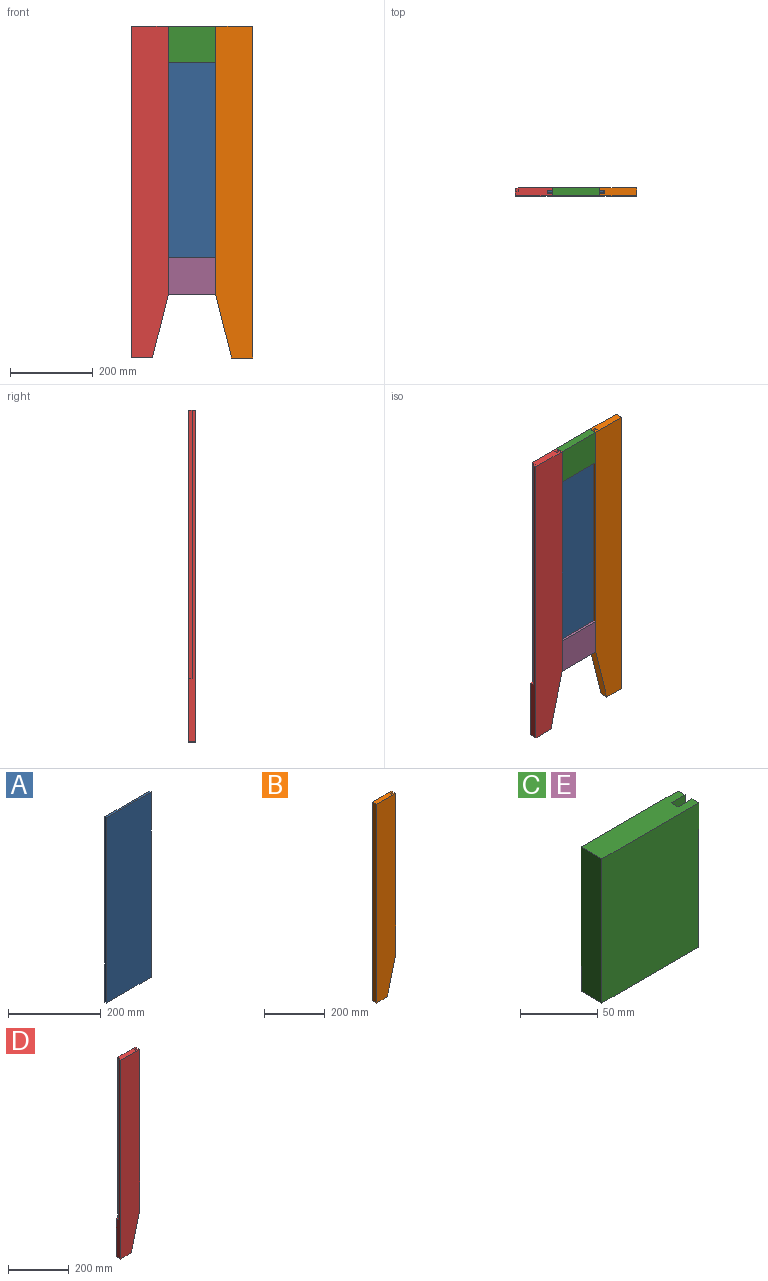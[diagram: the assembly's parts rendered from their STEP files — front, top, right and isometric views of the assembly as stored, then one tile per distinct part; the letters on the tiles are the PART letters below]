
ASSEMBLY  parts=5 mates=4
PART A: 6 faces, bbox 136.5x5.1x489 mm
  f0: plane 136.53x5.08mm, normal (0,0,1), area 693.5mm2, adj f1,f3,f4,f5
  f1: plane 488.95x5.08mm, normal (-1,0,0), area 2483.9mm2, adj f0,f2,f4,f5
  f2: plane 136.53x5.08mm, normal (0,0,-1), area 693.5mm2, adj f1,f3,f4,f5
  f3: plane 488.95x5.08mm, normal (1,0,0), area 2483.9mm2, adj f0,f2,f4,f5
  f4: plane 488.95x136.53mm, normal (0,-1,0), area 66753.9mm2, adj f0,f1,f2,f3
  f5: plane 488.95x136.53mm, normal (0,1,0), area 66753.9mm2, adj f0,f1,f2,f3
PART B: 12 faces, bbox 88.9x19.1x800.1 mm
  f0: plane 647.7x6.35mm, normal (1,0,0), area 4112.9mm2, adj f3,f5,f7,f10
  f1: plane 50.8x19.05mm, normal (0,0,-1), area 967.7mm2, adj f2,f3,f6,f7
  f2: plane 800.1x88.9mm, normal (0,-1,0), area 68225.7mm2, adj f1,f4,f5,f6,f7
  f3: plane 800.1x88.9mm, normal (0,1,0), area 68225.7mm2, adj f0,f1,f5,f6,f7
  f4: plane 647.7x6.35mm, normal (1,0,0), area 4112.9mm2, adj f2,f5,f7,f8
  f5: plane 88.9x19.05mm, normal (0,0,1), area 1612.9mm2, adj f0,f2,f3,f4,f6,f8,f10,f11
  f6: plane 800.1x19.05mm, normal (-1,0,0), area 15241.9mm2, adj f1,f2,f3,f5
  f7: plane 152.4x38.1mm, normal (0.97,0,-0.24), area 2992.6mm2, adj f0,f1,f2,f3,f4,f9
  f8: plane 647.7x12.7mm, normal (0,1,0), area 8225.8mm2, adj f4,f5,f9,f11
  f9: plane 12.7x6.35mm, normal (0,0,1), area 80.6mm2, adj f7,f8,f10,f11
  f10: plane 647.7x12.7mm, normal (0,-1,0), area 8225.8mm2, adj f0,f5,f9,f11
  f11: plane 647.7x6.35mm, normal (1,0,0), area 4112.9mm2, adj f5,f8,f9,f10
PART C: 10 faces, bbox 88.9x19.1x114.3 mm
  f0: plane 114.3x6.35mm, normal (1,0,0), area 725.8mm2, adj f1,f3,f5,f7
  f1: plane 88.9x19.05mm, normal (0,0,-1), area 1612.9mm2, adj f0,f2,f4,f5,f6,f7,f8,f9
  f2: plane 114.3x6.35mm, normal (1,0,0), area 725.8mm2, adj f1,f3,f6,f8
  f3: plane 88.9x19.05mm, normal (0,0,1), area 1612.9mm2, adj f0,f2,f4,f5,f6,f7,f8,f9
  f4: plane 114.3x19.05mm, normal (-1,0,0), area 2177.4mm2, adj f1,f3,f5,f6
  f5: plane 114.3x88.9mm, normal (0,-1,0), area 10161.3mm2, adj f0,f1,f3,f4
  f6: plane 114.3x88.9mm, normal (0,1,0), area 10161.3mm2, adj f1,f2,f3,f4
  f7: plane 114.3x12.7mm, normal (0,1,0), area 1451.6mm2, adj f0,f1,f3,f9
  f8: plane 114.3x12.7mm, normal (0,-1,0), area 1451.6mm2, adj f1,f2,f3,f9
  f9: plane 114.3x6.35mm, normal (1,0,0), area 725.8mm2, adj f1,f3,f7,f8
PART D: 15 faces, bbox 88.9x19.1x800.1 mm
  f0: plane 800.1x88.9mm, normal (0,1,0), area 64112.8mm2, adj f1,f2,f5,f6,f7,f12,f13
  f1: plane 647.7x6.35mm, normal (1,0,0), area 4112.9mm2, adj f0,f5,f7,f10
  f2: plane 50.8x19.05mm, normal (0,0,-1), area 967.7mm2, adj f0,f3,f6,f7
  f3: plane 800.1x88.9mm, normal (0,-1,0), area 68225.7mm2, adj f2,f4,f5,f6,f7
  f4: plane 647.7x6.35mm, normal (1,0,0), area 4112.9mm2, adj f3,f5,f7,f8
  f5: plane 88.9x19.05mm, normal (0,0,1), area 1552.4mm2, adj f0,f1,f3,f4,f6,f8,f10,f11
  f6: plane 800.1x19.05mm, normal (-1,0,0), area 9072.6mm2, adj f0,f2,f3,f5,f13,f14
  f7: plane 152.4x38.1mm, normal (0.97,0,-0.24), area 2992.6mm2, adj f0,f1,f2,f3,f4,f9
  f8: plane 647.7x12.7mm, normal (0,1,0), area 8225.8mm2, adj f4,f5,f9,f11
  f9: plane 12.7x6.35mm, normal (0,0,1), area 80.6mm2, adj f7,f8,f10,f11
  f10: plane 647.7x12.7mm, normal (0,-1,0), area 8225.8mm2, adj f1,f5,f9,f11
  f11: plane 647.7x6.35mm, normal (1,0,0), area 4112.9mm2, adj f5,f8,f9,f10
  f12: plane 647.7x9.53mm, normal (-1,0,0), area 6169.3mm2, adj f0,f5,f13,f14
  f13: plane 9.53x6.35mm, normal (0,0,1), area 60.5mm2, adj f0,f6,f12,f14
  f14: plane 647.7x6.35mm, normal (0,1,0), area 4112.9mm2, adj f5,f6,f12,f13
PART E: same geometry as C
PLACE A t=(-157.35,-154.58,67.21)mm
PLACE B rot(axis=(0,0,1),180deg) t=(-54.16,-154.58,-8.99)mm
PLACE C rot(axis=(0,1,0),90deg) t=(-155.76,-154.58,346.61)mm
PLACE D t=(-257.36,-154.58,-8.99)mm
PLACE E rot(axis=(-0.71,0,-0.71),180deg) t=(-155.76,-154.58,-212.19)mm
MATE fastened E.f1 <-> D.f4  axis (-1,0,0) through (-212.91,-164.11,-256.64)mm
MATE fastened A.f1 <-> D.f11  axis (-1,0,0) through (-225.61,-154.58,67.21)mm
MATE fastened C.f1 <-> D.f4  axis (-1,0,0) through (-212.91,-164.11,391.06)mm
MATE fastened B.f4 <-> C.f3  axis (-1,0,0) through (-98.61,-145.06,391.06)mm
